# Revit family: Serene_T&T_Window_A_Standard
name_source: partatom
category: Windows
revit_build: Autodesk Revit 2014 (Build: 20130308_1515(x64)
units: mm (PartAtom-declared; Revit-internal decimal feet)

## types (6) — shared parameters
Custom Window Width = 590 mm  [stored 1.9357 ft]
DG Gasket Finish = Double Glazing Gasket Material
DG Gasket Thickness = 12 mm  [stored 0.0393701 ft]
DG Thickness Calc = 4 mm  [stored 0.0131234 ft]
Default Sill Height = 800 mm  [stored 2.62467 ft]
Description = Tilt and turn window, Type A
Frame Thickness = 52 mm
Limit Sash Height Max = 1500 mm  [stored 4.92126 ft]
Limit Sash Height Min = 300 mm
Limit Sash Width Max = 700 mm  [stored 2.29659 ft]
Limit Sash Width Min = 300 mm
Limit Window Height Max = 1568 mm  [stored 5.14436 ft]
Limit Window Height Min = 368 mm  [stored 1.20735 ft]
Limit Window Width Max = 768 mm  [stored 2.51969 ft]
Limit Window Width Min = 368 mm  [stored 1.20735 ft]
Manufacturer = Crealco
Max System DG One Piece Thickness = 4 mm  [stored 0.0131234 ft]
Max System DG Unit Thickness = 20 mm  [stored 0.0656168 ft]
Model = Serene
Sash Edge Gap = 34 mm
Sash Frame Gasket = 3 mm  [stored 0.00984252 ft]
Sash Width = 522 mm  [stored 1.7126 ft]
URL = http://www.crealco.co.za
Wall Closure = By host
Width = 590 mm  [stored 1.9357 ft]
zero-valued in all types: Custom Window Exterior Offset

## per-type parameters (varying)
| type | Clearvue Insulated LowE SHGC Value | Clearvue Insulated LowE U Value | Clearvue Insulated SHGC Value | Clearvue Insulated U Value | Clearvue SHGC Value | Clearvue U Value | Custom Windload | Custom Window Height | Energy Advantage SHGC Value | Energy Advantage U Value | Height | Intruderprufe LowE SHGC Value | Intruderprufe LowE U Value | Intruderprufe SHGC Value | Intruderprufe U Value | Max Pane Area | Sash Height | Windload Design |
| 52TT-0609S-1000Pa | 0.382 | 4.47 | 0.418 | 4.85 | 0.465 | 6.62 | 1000 mm  [stored 3.28084 ft] | 890 mm  [stored 2.91995 ft] | 0.419 | 5.7 | 890 mm  [stored 2.91995 ft] | 0.383 | 4.83 | 0.432 | 6.5 | 0.3 m² | 822 mm  [stored 2.69685 ft] | 1000 mm  [stored 3.28084 ft] |
| 52TT-0609S-1500Pa | 0.382 | 4.47 | 0.418 | 4.85 | 0.465 | 6.62 | 1500 mm  [stored 4.92126 ft] | 890 mm  [stored 2.91995 ft] | 0.419 | 5.7 | 890 mm  [stored 2.91995 ft] | 0.383 | 4.83 | 0.432 | 6.5 | 0.3 m² | 822 mm  [stored 2.69685 ft] | 1500 mm  [stored 4.92126 ft] |
| 52TT-0609S-2000Pa | 0.382 | 4.47 | 0.418 | 4.85 | 0.465 | 6.62 | 2000 mm  [stored 6.56168 ft] | 890 mm  [stored 2.91995 ft] | 0.419 | 5.7 | 890 mm  [stored 2.91995 ft] | 0.383 | 4.83 | 0.432 | 6.5 | 0.3 m² | 822 mm  [stored 2.69685 ft] | 2000 mm  [stored 6.56168 ft] |
| 52TT-0612S-1000Pa | 0.405 | 4.28 | 0.444 | 4.69 | 0.494 | 6.55 | 1000 mm  [stored 3.28084 ft] | 1190 mm  [stored 3.9042 ft] | 0.445 | 5.54 | 1190 mm  [stored 3.9042 ft] | 0.407 | 4.77 | 0.459 | 6.42 | 0.43 m² | 1122 mm  [stored 3.6811 ft] | 1000 mm  [stored 3.28084 ft] |
| 52TT-0612S-1500Pa | 0.405 | 4.28 | 0.444 | 4.69 | 0.494 | 6.55 | 1500 mm  [stored 4.92126 ft] | 1190 mm  [stored 3.9042 ft] | 0.445 | 5.54 | 1190 mm  [stored 3.9042 ft] | 0.407 | 4.77 | 0.459 | 6.42 | 0.43 m² | 1122 mm  [stored 3.6811 ft] | 1500 mm  [stored 4.92126 ft] |
| 52TT-0612S-2000Pa | 0.405 | 4.28 | 0.444 | 4.69 | 0.494 | 6.55 | 2000 mm  [stored 6.56168 ft] | 1190 mm  [stored 3.9042 ft] | 0.445 | 5.54 | 1190 mm  [stored 3.9042 ft] | 0.407 | 4.77 | 0.459 | 6.42 | 0.43 m² | 1122 mm  [stored 3.6811 ft] | 2000 mm  [stored 6.56168 ft] |

note: [stored X ft] marks values corroborated as IEEE doubles in the binary element streams (Revit-internal decimal feet)

## geometry (parser evidence)
native form markers: Sweep x17
no freeform markers — native parametric forms only
